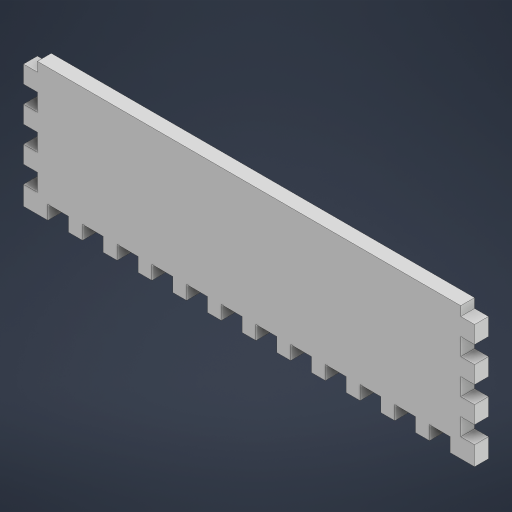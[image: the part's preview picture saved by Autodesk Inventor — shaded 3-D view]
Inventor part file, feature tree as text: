
AUTODESK INVENTOR PART (.ipt)
format: ipt  version: 2023 (Build 270158030, 158C)  size: 238,592 bytes
history: native  units: mm
features: extrude x1, sketch x1
ambient origin geometry x8: Origin, YZ Plane, XZ Plane, XY Plane, X Axis, Y Axis, Z Axis, Center Point
bodies: Solid1 (feature_tree)
feature tree (2):
  extrude  "Extrusion1"  [1 undecoded]
  sketch  "Sketch1"  dims[d0=4.0mm d1=0.0mm]
note: 1 required parameter value undecoded (feature->parameter linkage not recoverable at this tier; creation-order binding heuristic only, values carry confidence <= 0.55)
